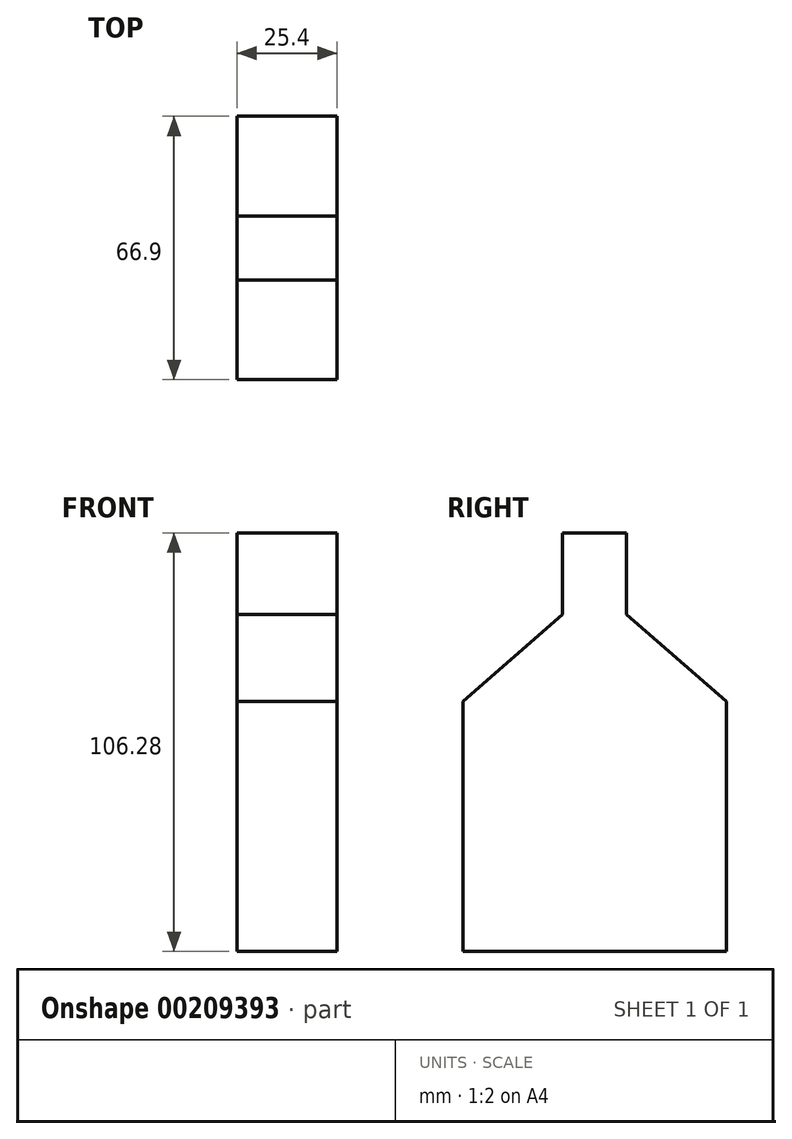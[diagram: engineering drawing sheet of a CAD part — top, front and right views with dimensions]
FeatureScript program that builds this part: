
annotation { "Feature Type Name" : "Feature", "Feature Type Description" : "" }
export const myFeature = defineFeature(function(context is Context, id is Id, definition is map)
    precondition{}
    {
        {
            var Q0;
            Q0=qCreatedBy(makeId("Right.planeOp"),FACE);
            var sketch = newSketch(context, id + "F0", { "sketchPlane" : qUnion([Q0])});
            skPoint(sketch, "E0.middle", {"position": v(0, -37.67) * mm});
            skPoint(sketch, "E1.end.orphan", {"position": v(0, 43.92) * mm});
            skPoint(sketch, "E0.left.end.orphan", {"position": v(-54.7, -11.1) * mm});
            skPoint(sketch, "E0.bottom.start.orphan", {"position": v(-54.7, -64.24) * mm});
            skPoint(sketch, "E0.right.end.orphan", {"position": v(54.7, -11.1) * mm});
            skPoint(sketch, "E0.right.start.orphan", {"position": v(54.7, -64.24) * mm});
            skLineSegment(sketch, "E2", {"start": v(0, -56.42) * mm, "end": v(33.45, -56.42) * mm});
            skLineSegment(sketch, "E3", {"start": v(33.45, -56.42) * mm, "end": v(33.45, 7.03) * mm});
            skLineSegment(sketch, "E4", {"start": v(33.45, 7.03) * mm, "end": v(8.13, 29.23) * mm});
            skLineSegment(sketch, "E5", {"start": v(8.13, 29.23) * mm, "end": v(8.13, 49.86) * mm});
            skLineSegment(sketch, "E6", {"start": v(8.13, 49.86) * mm, "end": v(0, 49.86) * mm});
            skLineSegment(sketch, "E7.MirrorCS", {"start": v(-8.13, 49.86) * mm, "end": v(0, 49.86) * mm});
            skLineSegment(sketch, "E8.MirrorCS", {"start": v(-8.13, 29.23) * mm, "end": v(-8.13, 49.86) * mm});
            skLineSegment(sketch, "E9.MirrorCS", {"start": v(-33.45, 7.03) * mm, "end": v(-8.13, 29.23) * mm});
            skLineSegment(sketch, "E10.MirrorCS", {"start": v(-33.45, -56.42) * mm, "end": v(-33.45, 7.03) * mm});
            skLineSegment(sketch, "E11.MirrorCS", {"start": v(0, -56.42) * mm, "end": v(-33.45, -56.42) * mm});
            skSolve(sketch);
        }
        {
            var Q0;
            Q0=makeQuery(id+"F0.imprint","IMPRINT",FACE,{"disambiguationData":[TD([[makeQuery(id+"F0.imprint","IMPRINT",EDGE,{"derivedFrom":sQuery(id+"F0.wireOp",EDGE,"E2")}),1.0]])]});
            extrude(context, id + "F1", {"entities" : qUnion([Q0]), "endBound" : BoundingType.SYMMETRIC, "depth" : 25.4 * mm});
        }
    });
